# Revit family: Поли-Групп_ЗадвижкаКлиноваяEAZ-EК-F5_DN1000-1200
name_source: partatom
category: Арматура трубопроводов
units: mm (PartAtom-declared; Revit-internal decimal feet)

## family parameters
Всегда вертикально = Да
На основе рабочей плоскости = Нет
Общий = Нет
При загрузке вырезать с полостями = Нет
Размер круглого соединителя = Использовать диаметр
Тип детали = Клапан - Вставляется

## types (4) — shared parameters
ADSK_URL страницы изделия = https://www.polycorr.ru
ADSK_Версия Revit = 2019
ADSK_Единица измерения = шт
ADSK_Завод-изготовитель = ООО ПК «Поли-Групп»
ADSK_Количество = 1
ADSK_Материал = Высокопрочный чугун GGG-40
ADSK_Материал наименование = Высокопрочный чугун с шаровидным графитом (GGG-40)
Kv = 1.0 м³/ч
f = 5 мм
Класс герметичности = А по ГОСТ Р 9544-2015
Материал Диска = Высокопрочный чугун с шаровидным графитом (GGG-40)
Материал уплотнителя = PTFE
Назначение = Для установки в качестве запорного устройства на трубопроводах
Покрытие = Высококачественное эпоксидное покрытие толщиной 300 мкм
Рабочая среда = Техническая вода, канализационные стоки, морская вода
Разработчик = https://3dbim.pro
Срок службы = 50 лет
ТВ = Поли-Групп_ЗадвижкаКлиноваяEAZ-EК-F5_DN1000-1200
Температура рабочей среды = 0 до +70°С
Тип привода = Редуктор
Тип присоединения = Фланцевое
с = 1 мм

## per-type parameters (varying)
- 1000-16: A=1468 мм; ADSK_Марка=EAZ-GV-4-F5 DN1000 PN16; ADSK_Масса=3050; ADSK_Масса_Текст=3050; ADSK_Наименование=Задвижка с обрезиненным клином EAZ EK F5 для воды с мягким уплотнением фланцевая маховик DN1000 PN16; ADSK_Наименование краткое=Задвижка клиновая EAZ EK F5 DN1000 PN16; D=1255 мм; D1=1170 мм; D2=1115 мм; DN=1000 мм; D_Наружный=1009 мм; H1=628 мм; H2=1825 мм; L=1200 мм; L1=700 мм; PN=16.0 бары; R=39 мм; R1=390 мм; b=50 мм; d1=250 мм; h2=1095 мм; l1=720 мм; l2=780 мм; l3=1080 мм; t=110 мм; Габаритные размеры=1200х1255х1825; Корпус_Глубина=1174 мм
- 1200-16: A=1625 мм; ADSK_Марка=EAZ-GV-4-F5 DN1200 PN16; ADSK_Масса=4660; ADSK_Масса_Текст=4660; ADSK_Наименование=Задвижка с обрезиненным клином EAZ EK F5 для воды с мягким уплотнением фланцевая маховик DN1200 PN16; ADSK_Наименование краткое=Задвижка клиновая EAZ EK F5 DN1200 PN16; D=1485 мм; D1=1390 мм; D2=1115 мм; DN=1200 мм; D_Наружный=1209 мм; H1=743 мм; H2=2294 мм; L=1400 мм; L1=800 мм; PN=16.0 бары; R=43 мм; R1=430 мм; b=57 мм; d1=300 мм; h2=1376 мм; l1=840 мм; l2=910 мм; l3=1260 мм; t=138 мм; Габаритные размеры=1400х1485х2294; Корпус_Глубина=1300 мм
- 1000-10: A=1468 мм; ADSK_Марка=EAZ-GV-4-F5 DN1000 PN10; ADSK_Масса=3050; ADSK_Масса_Текст=нет данных; ADSK_Наименование=Задвижка с обрезиненным клином EAZ EK F5 для воды с мягким уплотнением фланцевая маховик DN1000 PN10; ADSK_Наименование краткое=Задвижка клиновая EAZ EK F5 DN1000 PN10; D=1255 мм; D1=1160 мм; D2=1112 мм; DN=1000 мм; D_Наружный=1009 мм; H1=628 мм; H2=1825 мм; L=1200 мм; L1=700 мм; PN=10.0 бары; R=39 мм; R1=390 мм; b=50 мм; d1=250 мм; h2=1095 мм; l1=720 мм; l2=780 мм; l3=1080 мм; t=110 мм; Габаритные размеры=1200х1255х1825; Корпус_Глубина=1174 мм
- 1200-10: A=1625 мм; ADSK_Марка=EAZ-GV-4-F5 DN1200 PN10; ADSK_Масса=4660; ADSK_Масса_Текст=нет данных; ADSK_Наименование=Задвижка с обрезиненным клином EAZ EK F5 для воды с мягким уплотнением фланцевая маховик DN1200 PN10; ADSK_Наименование краткое=Задвижка клиновая EAZ EK F5 DN1200 PN10; D=1485 мм; D1=1380 мм; D2=1112 мм; DN=1200 мм; D_Наружный=1209 мм; H1=743 мм; H2=2294 мм; L=1400 мм; L1=800 мм; PN=10.0 бары; R=43 мм; R1=430 мм; b=57 мм; d1=300 мм; h2=1376 мм; l1=840 мм; l2=910 мм; l3=1260 мм; t=138 мм; Габаритные размеры=1400х1485х2294; Корпус_Глубина=1300 мм
